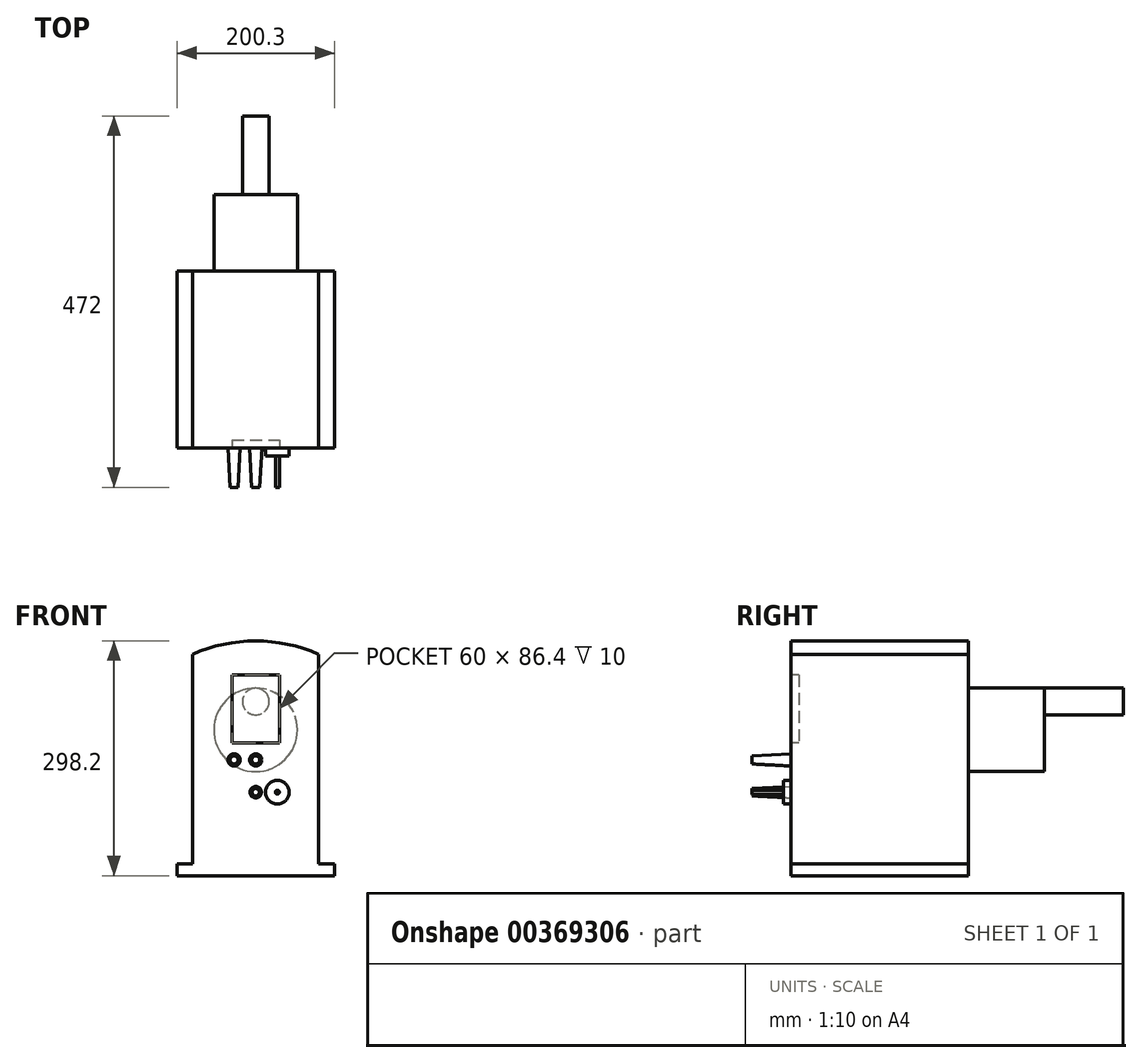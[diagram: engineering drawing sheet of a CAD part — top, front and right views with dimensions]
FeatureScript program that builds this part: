
annotation { "Feature Type Name" : "Feature", "Feature Type Description" : "" }
export const myFeature = defineFeature(function(context is Context, id is Id, definition is map)
    precondition{}
    {
        {
            var Q0;
            Q0=qCreatedBy(makeId("Front.planeOp"),FACE);
            var sketch = newSketch(context, id + "F0", { "sketchPlane" : qUnion([Q0])});
            skLineSegment(sketch, "E0", {"start": v(-72.7, -49.51) * mm, "end": v(127.6, -49.51) * mm});
            skLineSegment(sketch, "E1", {"start": v(127.6, -49.51) * mm, "end": v(127.6, -34.51) * mm});
            skLineSegment(sketch, "E2", {"start": v(127.6, -34.51) * mm, "end": v(107.6, -34.51) * mm});
            skLineSegment(sketch, "E3", {"start": v(107.6, -34.51) * mm, "end": v(107.6, 231.69) * mm});
            skLineSegment(sketch, "E4", {"start": v(107.6, 231.69) * mm, "end": v(-52.7, 231.69) * mm});
            skLineSegment(sketch, "E5", {"start": v(-52.7, 231.69) * mm, "end": v(-52.7, -34.51) * mm});
            skLineSegment(sketch, "E6", {"start": v(-52.7, -34.51) * mm, "end": v(-72.7, -34.51) * mm});
            skLineSegment(sketch, "E7", {"start": v(-72.7, -34.51) * mm, "end": v(-72.7, -49.51) * mm});
            skArc(sketch, "E8", {"start": v(107.6, 231.69) * mm, "mid": v(27.45, 248.69) * mm, "end": v(-52.7, 231.69) * mm});
            skCircle(sketch, "E9", {"center": v(0, 97.49) * mm, "radius": 7.75 * mm});
            skCircle(sketch, "E10", {"center": v(27.5, 97.49) * mm, "radius": 7.75 * mm});
            skCircle(sketch, "E11", {"center": v(27.5, 56.49) * mm, "radius": 7.25 * mm});
            skCircle(sketch, "E12", {"center": v(55, 56.49) * mm, "radius": 15 * mm});
            skLineSegment(sketch, "E13", {"start": v(0, 97.49) * mm, "end": v(27.5, 97.49) * mm, "construction": true});
            skLineSegment(sketch, "E14", {"start": v(27.5, 56.49) * mm, "end": v(55, 56.49) * mm, "construction": true});
            skLineSegment(sketch, "E15.bottom", {"start": v(-2.5, 205.49) * mm, "end": v(57.5, 205.49) * mm});
            skLineSegment(sketch, "E15.top", {"start": v(-2.5, 119.09) * mm, "end": v(57.5, 119.09) * mm});
            skLineSegment(sketch, "E15.left", {"start": v(-2.5, 205.49) * mm, "end": v(-2.5, 119.09) * mm});
            skLineSegment(sketch, "E15.right", {"start": v(57.5, 205.49) * mm, "end": v(57.5, 119.09) * mm});
            skSolve(sketch);
        }
        {
            var Q0;
            Q0=makeQuery(id+"F0.imprint","IMPRINT",FACE,{"disambiguationData":[TD([[makeQuery(id+"F0.imprint","IMPRINT",EDGE,{"derivedFrom":sQuery(id+"F0.wireOp",EDGE,"E0")}),1.0]])]});
            var Q1;
            Q1=makeQuery(id+"F0.imprint","IMPRINT",FACE,{"disambiguationData":[TD([[makeQuery(id+"F0.imprint","IMPRINT",EDGE,{"derivedFrom":sQuery(id+"F0.wireOp",EDGE,"E4")}),-1.0]])]});
            var Q2;
            Q2=makeQuery(id+"F0.imprint","IMPRINT",FACE,{"disambiguationData":[TD([[makeQuery(id+"F0.imprint","IMPRINT",EDGE,{"derivedFrom":sQuery(id+"F0.wireOp",EDGE,"E15.bottom")}),-1.0]])]});
            var Q3;
            Q3=makeQuery(id+"F0.imprint","IMPRINT",FACE,{"disambiguationData":[TD([[makeQuery(id+"F0.imprint","IMPRINT",EDGE,{"derivedFrom":sQuery(id+"F0.wireOp",EDGE,"E9")}),1.0]])]});
            var Q4;
            Q4=makeQuery(id+"F0.imprint","IMPRINT",FACE,{"disambiguationData":[TD([[makeQuery(id+"F0.imprint","IMPRINT",EDGE,{"derivedFrom":sQuery(id+"F0.wireOp",EDGE,"E10")}),1.0]])]});
            var Q5;
            Q5=makeQuery(id+"F0.imprint","IMPRINT",FACE,{"disambiguationData":[TD([[makeQuery(id+"F0.imprint","IMPRINT",EDGE,{"derivedFrom":sQuery(id+"F0.wireOp",EDGE,"E12")}),1.0]])]});
            var Q6;
            Q6=makeQuery(id+"F0.imprint","IMPRINT",FACE,{"disambiguationData":[TD([[makeQuery(id+"F0.imprint","IMPRINT",EDGE,{"derivedFrom":sQuery(id+"F0.wireOp",EDGE,"E11")}),1.0]])]});
            extrude(context, id + "F1", {"entities" : qUnion([Q0, Q1, Q2, Q3, Q4, Q5, Q6]), "oppositeDirection" : true, "depth" : 225 * mm});
        }
        {
            var Q0;
            Q0=makeQuery(id+"F0.imprint","IMPRINT",FACE,{"disambiguationData":[TD([[makeQuery(id+"F0.imprint","IMPRINT",EDGE,{"derivedFrom":sQuery(id+"F0.wireOp",EDGE,"E9")}),1.0]])]});
            var Q1;
            Q1=makeQuery(id+"F0.imprint","IMPRINT",FACE,{"disambiguationData":[TD([[makeQuery(id+"F0.imprint","IMPRINT",EDGE,{"derivedFrom":sQuery(id+"F0.wireOp",EDGE,"E10")}),1.0]])]});
            extrude(context, id + "F2", {"entities" : qUnion([Q0, Q1]), "operationType" : NewBodyOperationType.ADD, "depth" : 50 * mm, "hasDraft" : true, "draftAngle" : 3 * degree, "draftPullDirection" : true});
        }
        {
            var Q0;
            Q0=makeQuery(id+"F0.imprint","IMPRINT",FACE,{"disambiguationData":[TD([[makeQuery(id+"F0.imprint","IMPRINT",EDGE,{"derivedFrom":sQuery(id+"F0.wireOp",EDGE,"E11")}),1.0]])]});
            extrude(context, id + "F3", {"entities" : qUnion([Q0]), "operationType" : NewBodyOperationType.ADD, "depth" : 50 * mm, "hasDraft" : true, "draftAngle" : 3 * degree, "draftPullDirection" : true});
        }
        {
            var Q0;
            Q0=makeQuery(id+"F0.imprint","IMPRINT",FACE,{"disambiguationData":[TD([[makeQuery(id+"F0.imprint","IMPRINT",EDGE,{"derivedFrom":sQuery(id+"F0.wireOp",EDGE,"E15.bottom")}),-1.0]])]});
            extrude(context, id + "F4", {"entities" : qUnion([Q0]), "operationType" : NewBodyOperationType.REMOVE, "oppositeDirection" : true, "depth" : 10 * mm});
        }
        {
            var Q0;
            Q0=makeQuery(id+"F0.imprint","IMPRINT",FACE,{"disambiguationData":[TD([[makeQuery(id+"F0.imprint","IMPRINT",EDGE,{"derivedFrom":sQuery(id+"F0.wireOp",EDGE,"E12")}),1.0]])]});
            extrude(context, id + "F5", {"entities" : qUnion([Q0]), "operationType" : NewBodyOperationType.ADD, "depth" : 10 * mm});
        }
        {
            var Q0;
            Q0=makeQuery(id+"F5.opExtrude","CAP_FACE",FACE,{"disambiguationData":[OSD([sQuery(id+"F0.wireOp",EDGE,"E12")])],"isStart":false});
            var sketch = newSketch(context, id + "F6", { "sketchPlane" : qUnion([Q0])});
            skCircle(sketch, "E16.0", {"center": v(55, 56.49) * mm, "radius": 15 * mm, "construction": true});
            skCircle(sketch, "E17", {"center": v(55, 56.49) * mm, "radius": 2.5 * mm});
            skSolve(sketch);
        }
        {
            var Q0;
            Q0=makeQuery(id+"F6.imprint","IMPRINT",FACE,{"disambiguationData":[TD([[makeQuery(id+"F6.imprint","IMPRINT",EDGE,{"derivedFrom":sQuery(id+"F6.wireOp",EDGE,"E17")}),1.0]])]});
            var Q1;
            Q1=sQuery(id+"F6.wireOp",EDGE,"E17");
            extrude(context, id + "F7", {"entities" : qUnion([Q0]), "operationType" : NewBodyOperationType.ADD, "surfaceEntities" : qUnion([Q1]), "depth" : 40 * mm});
        }
        {
            var Q0;
            Q0=makeQuery(id+"F1.opExtrude","CAP_FACE",FACE,{"disambiguationData":[OSD([sQuery(id+"F0.wireOp",EDGE,"E0"),sQuery(id+"F0.wireOp",EDGE,"E1"),sQuery(id+"F0.wireOp",EDGE,"E2"),sQuery(id+"F0.wireOp",EDGE,"E3"),sQuery(id+"F0.wireOp",EDGE,"E5"),sQuery(id+"F0.wireOp",EDGE,"E6"),sQuery(id+"F0.wireOp",EDGE,"E7"),sQuery(id+"F0.wireOp",EDGE,"E8")])],"isStart":false});
            var sketch = newSketch(context, id + "F8", { "sketchPlane" : qUnion([Q0])});
            skCircle(sketch, "E18", {"center": v(-27.4, 135.69) * mm, "radius": 53 * mm});
            skSolve(sketch);
        }
        {
            var Q0;
            Q0 = qSketchRegion(id + "F8", true);
            extrude(context, id + "F9", {"entities" : qUnion([Q0]), "operationType" : NewBodyOperationType.ADD, "depth" : 97 * mm});
        }
        {
            var Q0;
            Q0=makeQuery(id+"F9.opExtrude","CAP_FACE",FACE,{"disambiguationData":[OSD([sQuery(id+"F8.wireOp",EDGE,"E18")])],"isStart":false});
            var sketch = newSketch(context, id + "F10", { "sketchPlane" : qUnion([Q0])});
            skCircle(sketch, "E19", {"center": v(-27.5, 171.69) * mm, "radius": 17 * mm});
            skPoint(sketch, "E20.0", {"position": v(72.7, -49.51) * mm});
            skSolve(sketch);
        }
        {
            var Q0;
            Q0 = qSketchRegion(id + "F10", true);
            extrude(context, id + "F11", {"entities" : qUnion([Q0]), "operationType" : NewBodyOperationType.ADD, "depth" : 100 * mm});
        }
    });
